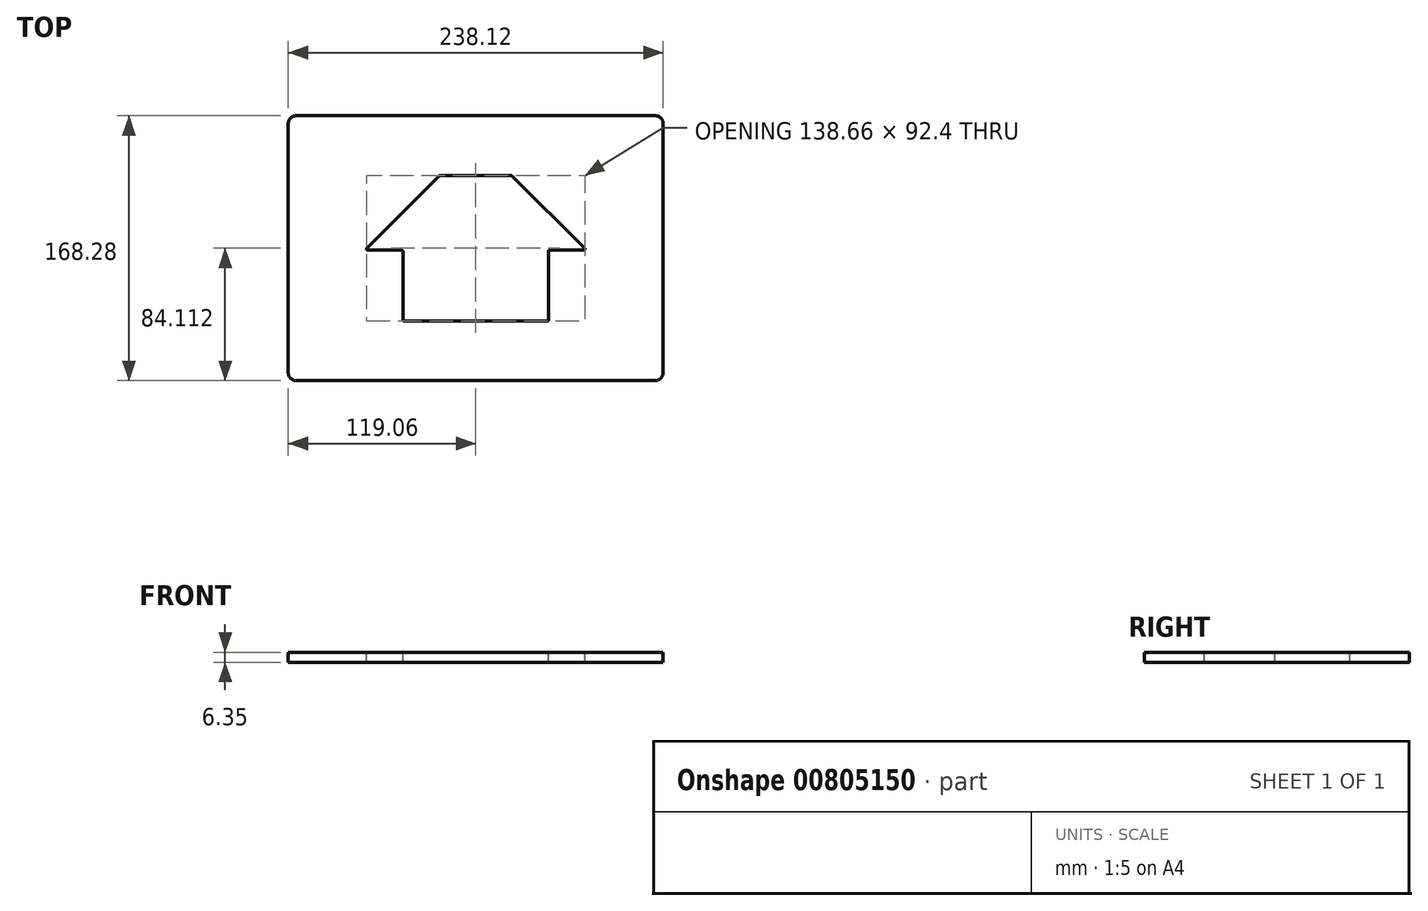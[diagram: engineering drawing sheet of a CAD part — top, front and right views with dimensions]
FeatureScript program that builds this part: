
annotation { "Feature Type Name" : "Feature", "Feature Type Description" : "" }
export const myFeature = defineFeature(function(context is Context, id is Id, definition is map)
    precondition{}
    {
        {
            var Q0;
            Q0=qCreatedBy(makeId("Top.planeOp"),FACE);
            var sketch = newSketch(context, id + "F0", { "sketchPlane" : qUnion([Q0])});
            skLineSegment(sketch, "E0.bottom", {"start": v(119.06, 84.14) * mm, "end": v(-119.06, 84.14) * mm});
            skLineSegment(sketch, "E0.top", {"start": v(119.06, -84.14) * mm, "end": v(-119.06, -84.14) * mm});
            skLineSegment(sketch, "E0.left", {"start": v(119.06, 84.14) * mm, "end": v(119.06, -84.14) * mm});
            skLineSegment(sketch, "E0.right", {"start": v(-119.06, 84.14) * mm, "end": v(-119.06, -84.14) * mm});
            skPoint(sketch, "E0.middle", {"position": v(0, 0) * mm});
            skSolve(sketch);
        }
        {
            var Q0;
            Q0 = qSketchRegion(id + "F0", true);
            extrude(context, id + "F1", {"entities" : qUnion([Q0]), "depth" : 6.35 * mm, "offsetDistance" : 25.4 * mm});
        }
        {
            var Q0;
            Q0=makeQuery(id+"F1.opExtrude","CAP_FACE",FACE,{"disambiguationData":[OSD([sQuery(id+"F0.wireOp",EDGE,"E0.bottom"),sQuery(id+"F0.wireOp",EDGE,"E0.top"),sQuery(id+"F0.wireOp",EDGE,"E0.left"),sQuery(id+"F0.wireOp",EDGE,"E0.right")])],"isStart":false});
            var sketch = newSketch(context, id + "F2", { "sketchPlane" : qUnion([Q0])});
            skLineSegment(sketch, "E1", {"start": v(0, 44.9) * mm, "end": v(-22.48, 44.9) * mm});
            skLineSegment(sketch, "E2", {"start": v(-22.48, 44.9) * mm, "end": v(-67.38, 0) * mm});
            skLineSegment(sketch, "E3", {"start": v(-67.38, 0) * mm, "end": v(-44.96, 0) * mm});
            skLineSegment(sketch, "E4", {"start": v(-44.96, 0) * mm, "end": v(-44.96, -44.96) * mm});
            skLineSegment(sketch, "E5", {"start": v(-44.96, -44.96) * mm, "end": v(0, -44.96) * mm});
            skLineSegment(sketch, "E6.MirrorCS", {"start": v(0, 44.9) * mm, "end": v(22.48, 44.9) * mm});
            skLineSegment(sketch, "E7.MirrorCS", {"start": v(22.48, 44.9) * mm, "end": v(67.38, 0) * mm});
            skLineSegment(sketch, "E8.MirrorCS", {"start": v(67.38, 0) * mm, "end": v(44.96, 0) * mm});
            skLineSegment(sketch, "E9.MirrorCS", {"start": v(44.96, 0) * mm, "end": v(44.96, -44.96) * mm});
            skLineSegment(sketch, "E10.MirrorCS", {"start": v(44.96, -44.96) * mm, "end": v(0, -44.96) * mm});
            skSolve(sketch);
        }
        {
            var Q0;
            Q0 = qSketchRegion(id + "F2", true);
            extrude(context, id + "F3", {"entities" : qUnion([Q0]), "operationType" : NewBodyOperationType.REMOVE, "endBound" : BoundingType.THROUGH_ALL, "oppositeDirection" : true, "depth" : 25.4 * mm, "offsetDistance" : 25.4 * mm});
        }
        {
            var Q0;
            Q0=makeQuery(id+"F1.opExtrude","CAP_FACE",FACE,{"disambiguationData":[OSD([sQuery(id+"F0.wireOp",EDGE,"E0.bottom"),sQuery(id+"F0.wireOp",EDGE,"E0.top"),sQuery(id+"F0.wireOp",EDGE,"E0.left"),sQuery(id+"F0.wireOp",EDGE,"E0.right")])],"isStart":false});
            var sketch = newSketch(context, id + "F4", { "sketchPlane" : qUnion([Q0])});
            skLineSegment(sketch, "E11.0", {"start": v(-23.24, 45.94) * mm, "end": v(-69.1, 0.07) * mm});
            skLineSegment(sketch, "E11.1", {"start": v(-68.55, -1.27) * mm, "end": v(-47.02, -1.27) * mm});
            skLineSegment(sketch, "E11.2", {"start": v(-22.68, 46.17) * mm, "end": v(22.68, 46.17) * mm});
            skLineSegment(sketch, "E11.3", {"start": v(-46.23, -2.06) * mm, "end": v(-46.23, -46.23) * mm});
            skLineSegment(sketch, "E11.4", {"start": v(23.24, 45.94) * mm, "end": v(69.1, 0.07) * mm});
            skLineSegment(sketch, "E11.5", {"start": v(68.55, -1.27) * mm, "end": v(46.23, -1.27) * mm});
            skLineSegment(sketch, "E11.6", {"start": v(46.23, -1.27) * mm, "end": v(46.23, -45.44) * mm});
            skLineSegment(sketch, "E11.7", {"start": v(45.44, -46.23) * mm, "end": v(-46.23, -46.23) * mm});
            skPoint(sketch, "E12.visualSharp", {"position": v(-23, 46.17) * mm});
            skArc(sketch, "E12.filletArc", {"start": v(-22.68, 46.17) * mm, "mid": v(-22.98, 46.11) * mm, "end": v(-23.24, 45.94) * mm});
            skPoint(sketch, "E13.visualSharp", {"position": v(-70.45, -1.27) * mm});
            skArc(sketch, "E13.filletArc", {"start": v(-69.1, 0.07) * mm, "mid": v(-69.27, -0.78) * mm, "end": v(-68.55, -1.27) * mm});
            skPoint(sketch, "E14.visualSharp", {"position": v(-46.23, -1.27) * mm});
            skArc(sketch, "E14.filletArc", {"start": v(-46.23, -2.06) * mm, "mid": v(-46.46, -1.5) * mm, "end": v(-47.02, -1.27) * mm});
            skPoint(sketch, "E15.visualSharp", {"position": v(46.23, -46.23) * mm});
            skArc(sketch, "E15.filletArc", {"start": v(45.44, -46.23) * mm, "mid": v(46, -46) * mm, "end": v(46.23, -45.44) * mm});
            skPoint(sketch, "E16.visualSharp", {"position": v(70.45, -1.27) * mm});
            skArc(sketch, "E16.filletArc", {"start": v(68.55, -1.27) * mm, "mid": v(69.27, -0.78) * mm, "end": v(69.1, 0.07) * mm});
            skPoint(sketch, "E17.visualSharp", {"position": v(23, 46.17) * mm});
            skArc(sketch, "E17.filletArc", {"start": v(23.24, 45.94) * mm, "mid": v(22.98, 46.11) * mm, "end": v(22.68, 46.17) * mm});
            skSolve(sketch);
        }
        {
            var Q0;
            Q0 = qSketchRegion(id + "F4", true);
            extrude(context, id + "F5", {"entities" : qUnion([Q0]), "operationType" : NewBodyOperationType.REMOVE, "endBound" : BoundingType.THROUGH_ALL, "oppositeDirection" : true, "depth" : 25.4 * mm, "offsetDistance" : 25.4 * mm});
        }
        {
            var Q0;
            Q0=makeQuery(id+"F1.opExtrude","SWEPT_EDGE",EDGE,{"disambiguationData":[OSD([sQuery(id+"F0.wireOp",EDGE,"E0.bottom"),sQuery(id+"F0.wireOp",EDGE,"E0.left")])]});
            var Q1;
            Q1=makeQuery(id+"F1.opExtrude","SWEPT_EDGE",EDGE,{"disambiguationData":[OSD([sQuery(id+"F0.wireOp",EDGE,"E0.top"),sQuery(id+"F0.wireOp",EDGE,"E0.left")])]});
            var Q2;
            Q2=makeQuery(id+"F1.opExtrude","SWEPT_EDGE",EDGE,{"disambiguationData":[OSD([sQuery(id+"F0.wireOp",EDGE,"E0.top"),sQuery(id+"F0.wireOp",EDGE,"E0.right")])]});
            var Q3;
            Q3=makeQuery(id+"F1.opExtrude","SWEPT_EDGE",EDGE,{"disambiguationData":[OSD([sQuery(id+"F0.wireOp",EDGE,"E0.bottom"),sQuery(id+"F0.wireOp",EDGE,"E0.right")])]});
            fillet(context, id + "F6", {"entities" : qUnion([Q0, Q1, Q2, Q3]), "radius" : 5.08 * mm, "tangentPropagation" : true, "allowEdgeOverflow" : false});
        }
    });
